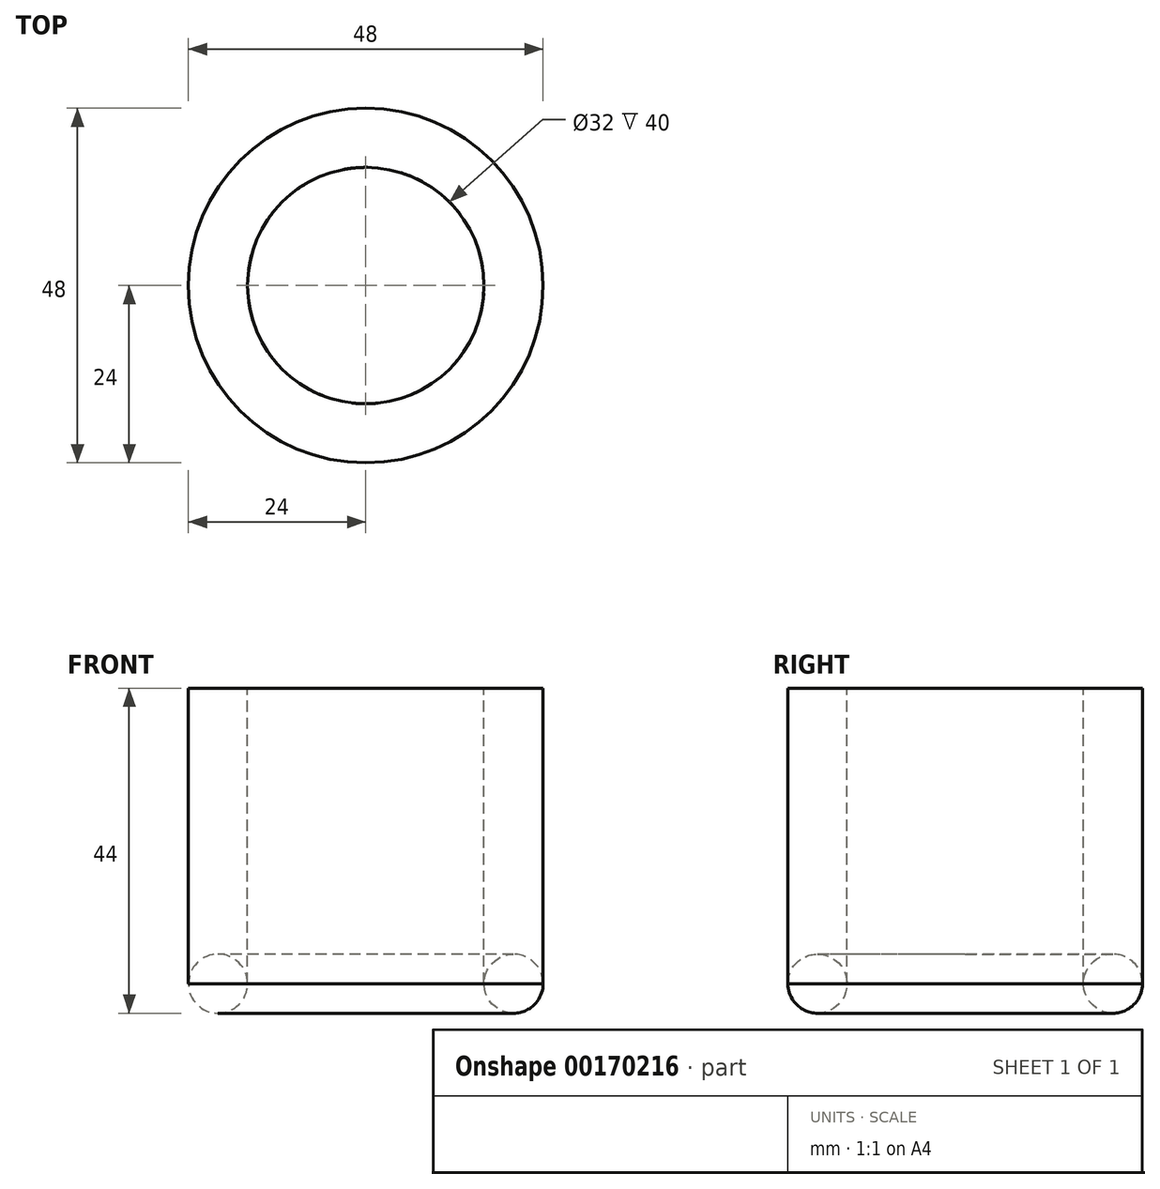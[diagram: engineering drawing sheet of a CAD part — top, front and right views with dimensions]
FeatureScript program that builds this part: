
annotation { "Feature Type Name" : "Feature", "Feature Type Description" : "" }
export const myFeature = defineFeature(function(context is Context, id is Id, definition is map)
    precondition{}
    {
        {
            var Q0;
            Q0=qCreatedBy(makeId("Front.planeOp"),FACE);
            var sketch = newSketch(context, id + "F0", { "sketchPlane" : qUnion([Q0])});
            skCircle(sketch, "E0", {"center": v(-20, 0) * mm, "radius": 4 * mm});
            skLineSegment(sketch, "E1", {"start": v(-20, 0) * mm, "end": v(0, 0) * mm, "construction": true});
            skLineSegment(sketch, "E2", {"start": v(0, 0) * mm, "end": v(0, 40) * mm});
            skSolve(sketch);
        }
        {
            var Q0;
            Q0=makeQuery(id+"F0.imprint","IMPRINT",FACE,{"disambiguationData":[TD([[makeQuery(id+"F0.imprint","IMPRINT",EDGE,{"derivedFrom":sQuery(id+"F0.wireOp",EDGE,"E0")}),1.0]])]});
            var Q1;
            Q1=sQuery(id+"F0.wireOp",EDGE,"E2");
            revolve(context, id + "F1", {"entities" : qUnion([Q0]), "axis" : qUnion([Q1]), "revolveType" : RevolveType.FULL});
        }
        {
            var Q0;
            Q0=qCreatedBy(makeId("Top.planeOp"),FACE);
            var sketch = newSketch(context, id + "F2", { "sketchPlane" : qUnion([Q0])});
            skCircle(sketch, "E3", {"center": v(0, 0) * mm, "radius": 24 * mm});
            skCircle(sketch, "E4", {"center": v(0, 0) * mm, "radius": 16 * mm});
            skSolve(sketch);
        }
        {
            var Q0;
            Q0 = qSketchRegion(id + "F2", true);
            var Q1;
            Q1=sQuery(id+"F0.wireOp",EDGE,"E2");
            sweep(context, id + "F3", {"profiles" : qUnion([Q0]), "path" : qUnion([Q1])});
        }
    });
